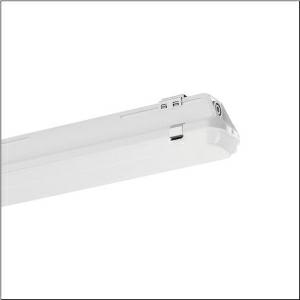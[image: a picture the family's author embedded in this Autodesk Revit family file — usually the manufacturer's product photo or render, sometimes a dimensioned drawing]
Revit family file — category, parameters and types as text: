
# Revit family: monsun_r__11_51fp11mp4b0u_7fbb
name_source: partatom
category: Lighting Fixtures
units: mm (PartAtom-declared; Revit-internal decimal feet)

## family parameters
Cut with Voids When Loaded = No
Host = Face
Light Source = No
Part Type = Normal
Room Calculation Point = No
Round Connector Dimension = Use Diameter
Shared = No

## types (1)
- --- (1 x LED, 11900 lm, 62.4 W, 4000K)
    Apparent Load = 62 VA
    CIE Flux Codes = 71 88 97 97 100
    Color Rendering = 80
    Color Temperature = 4000K
    Default Elevation = 1800 mm
    Description = Monsun® 11, damp-proof luminaire, chain hanger, primary optical cover: enclosure, of PMMA, light emission: direct distribution, primary light characteristic: symmetric, installation type: suspended mounting, surface-mounted, horizontal mounting, vertical mounting, LED, rated luminous flux: 11.900lm, luminous efficacy: 191lm/W, light colour: 840, colour temperature: 4000K, control gear: ON/OFF Multilumen, with terminal, 3-pole, max. 2.5mm², mains connection: 220..240V, AC, 50/60Hz, rated input power: 62W, luminaire housing, of glass-fibre reinforced polyester, uncoated, bright grey, incl. chain hanger, length: 1.590mm, width: 90mm, height: 88mm, clip for enclosure, of stainless steel (V2A), ceiling mounting element, of stainless steel (V2A), chain hanger, of stainless steel (V2A), protection rating (complete): IP66, insulation class (complete): insulation class I (protective earthing), certification: CE, ENEC, VDE, UKCA, protection symbol: D, impact resistance: IK04, permissible operating ambient temperature: -35..+35°C, standard: EN 50419, EN 60598-2-1, contact your sales advisor before using the luminaires in applications with unclear chemical exposure, large temperature fluctuations or condensation-forming humidity, LABS conformity tested according to VDMA 24364:2018-05, no direct snow, no direct sun, no direct rain, for indoor or canopied outdoor use, corresponds to IFS (International Featured Standards) requirements for safety and quality in the food industry, packaging unit: 1 piece
    Height = 89 mm
    Lamp = 1 x LED
    Lamp Light Flux = 11900 lm
    Lamp Power = 62.4 W
    Lamp count = 1
    Length = 1590 mm
    Luminous efficacy = 191 lm/W
    Manufacturer = Siteco
    ModVariant = No
    Model = 51FP11MP4B0U
    Mounting Place = Ceiling
    Mounting Type = Surface mounted
    Number of Poles = 1
    OnlyDefault = Yes
    Power Factor = 1
    Product Name = Monsun® 11
    Product group = damp-proof luminaire
    ProductGroupID = 300
    Protection Class = Protection class I
    Protection Degree = IP 66
    RLX_Detail_Level = 1
    RLX_Emergency_Light_Flux = 0 lm
    RLX_Emergency_Type = 0
    RLX_Emergency_Type_DB = No
    RlxData = <blob elided: 89901 chars, md5=840a08c7>
    Socket = socket
    Standby Power = 0 W
    System Light Flux = 11900 lm
    System Power = 62 W
    Type Comments = factory setting: luminous flux: 100 % | (A | C | E) | 147 mA
    Type Image = l_1349237.jpg
    URL = http://relux.com
    VarID = @adj_018644
    Voltage = 0 V
    Weight = 0.00 kg
    Width = 90 mm

## geometry (parser evidence)
native form markers: Blend x4, Sweep x10
no freeform markers — native parametric forms only
